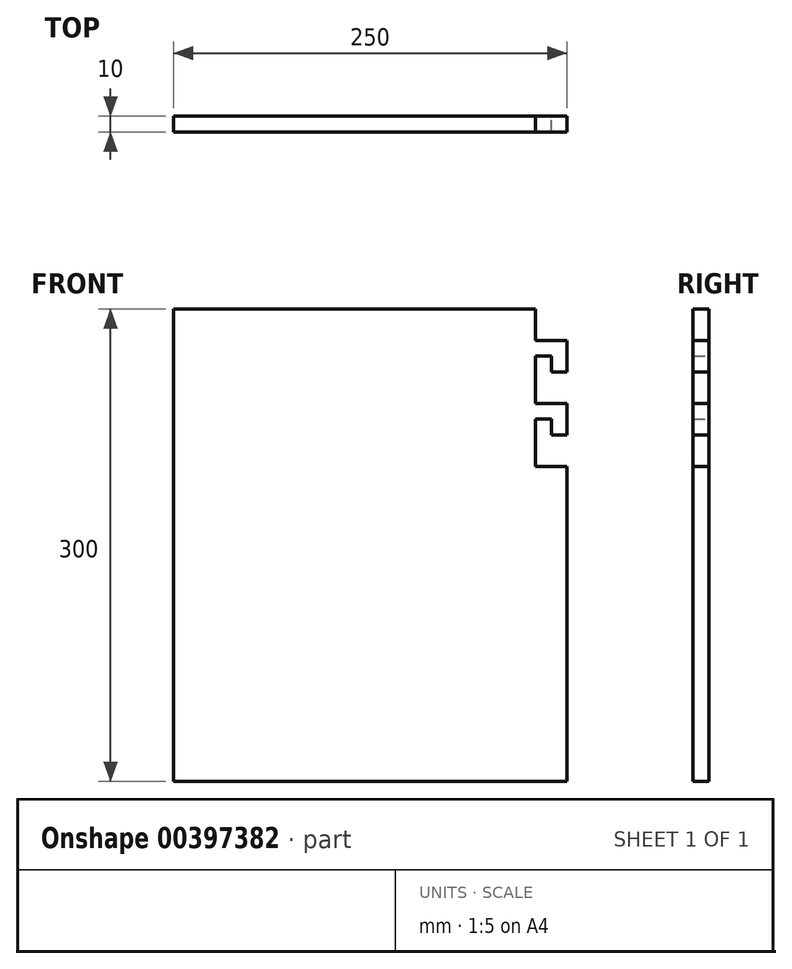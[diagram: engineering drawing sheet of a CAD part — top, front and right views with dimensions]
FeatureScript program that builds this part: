
annotation { "Feature Type Name" : "Feature", "Feature Type Description" : "" }
export const myFeature = defineFeature(function(context is Context, id is Id, definition is map)
    precondition{}
    {
        {
            var Q0;
            Q0=qCreatedBy(makeId("Front.planeOp"),FACE);
            var sketch = newSketch(context, id + "F0", { "sketchPlane" : qUnion([Q0])});
            skLineSegment(sketch, "E0", {"start": v(0, 0) * mm, "end": v(250, 0) * mm});
            skLineSegment(sketch, "E1", {"start": v(250, 0) * mm, "end": v(250, 200) * mm});
            skLineSegment(sketch, "E2", {"start": v(230, 300) * mm, "end": v(0, 300) * mm});
            skLineSegment(sketch, "E3", {"start": v(0, 300) * mm, "end": v(0, 0) * mm});
            skLineSegment(sketch, "E4", {"start": v(230, 300) * mm, "end": v(230, 280) * mm});
            skLineSegment(sketch, "E5", {"start": v(230, 280) * mm, "end": v(250, 280) * mm});
            skLineSegment(sketch, "E6", {"start": v(250, 280) * mm, "end": v(250, 260) * mm});
            skLineSegment(sketch, "E7", {"start": v(250, 260) * mm, "end": v(240, 260) * mm});
            skLineSegment(sketch, "E8", {"start": v(240, 260) * mm, "end": v(240, 270) * mm});
            skLineSegment(sketch, "E9", {"start": v(240, 270) * mm, "end": v(230, 270) * mm});
            skLineSegment(sketch, "E10", {"start": v(230, 270) * mm, "end": v(230, 240) * mm});
            skLineSegment(sketch, "E11", {"start": v(230, 240) * mm, "end": v(250, 240) * mm});
            skLineSegment(sketch, "E12", {"start": v(250, 240) * mm, "end": v(250, 220) * mm});
            skLineSegment(sketch, "E13", {"start": v(250, 220) * mm, "end": v(240, 220) * mm});
            skLineSegment(sketch, "E14", {"start": v(240, 220) * mm, "end": v(240, 230) * mm});
            skLineSegment(sketch, "E15", {"start": v(240, 230) * mm, "end": v(230, 230) * mm});
            skLineSegment(sketch, "E16", {"start": v(230, 230) * mm, "end": v(230, 200) * mm});
            skLineSegment(sketch, "E17", {"start": v(230, 200) * mm, "end": v(250, 200) * mm});
            skLineSegment(sketch, "E18.trimOffspring", {"start": v(250, 260) * mm, "end": v(250, 280) * mm});
            skLineSegment(sketch, "E19.trimOffspring", {"start": v(250, 220) * mm, "end": v(250, 240) * mm});
            skSolve(sketch);
        }
        {
            var Q0;
            Q0=makeQuery(id+"F0.imprint","IMPRINT",FACE,{"disambiguationData":[TD([[makeQuery(id+"F0.imprint","IMPRINT",EDGE,{"derivedFrom":sQuery(id+"F0.wireOp",EDGE,"E0")}),1.0]])]});
            extrude(context, id + "F1", {"entities" : qUnion([Q0]), "depth" : 10 * mm});
        }
    });
